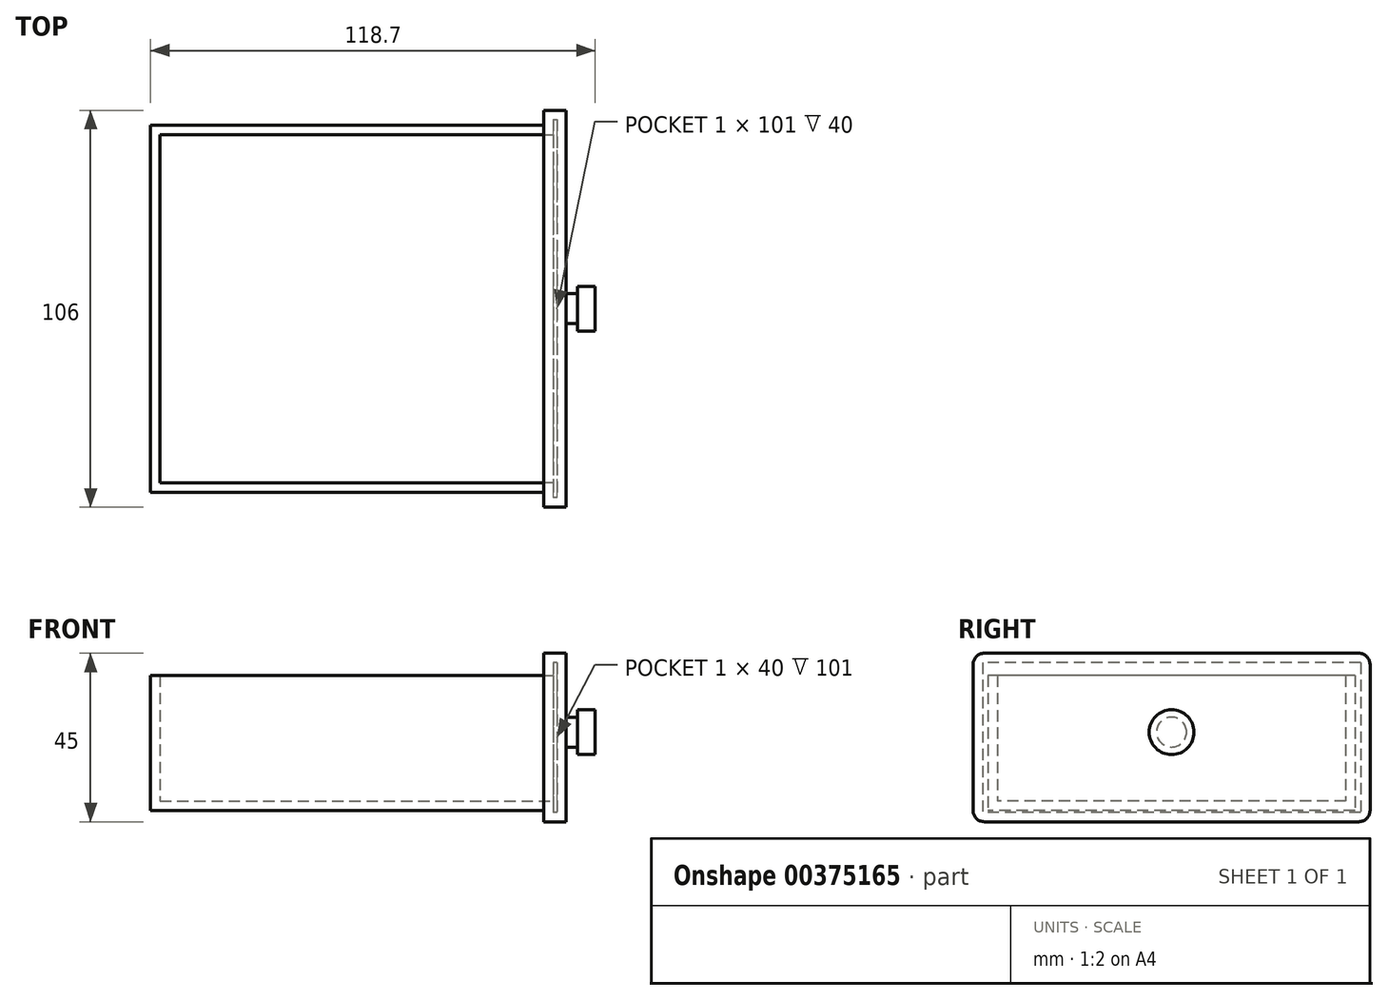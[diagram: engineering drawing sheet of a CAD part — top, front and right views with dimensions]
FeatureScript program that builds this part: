
annotation { "Feature Type Name" : "Feature", "Feature Type Description" : "" }
export const myFeature = defineFeature(function(context is Context, id is Id, definition is map)
    precondition{}
    {
        {
            var Q0;
            Q0=qCreatedBy(makeId("Top.planeOp"),FACE);
            var sketch = newSketch(context, id + "F0", { "sketchPlane" : qUnion([Q0])});
            skLineSegment(sketch, "E0", {"start": v(0, 49) * mm, "end": v(0, -49) * mm});
            skLineSegment(sketch, "E1", {"start": v(0, 49) * mm, "end": v(105, 49) * mm});
            skLineSegment(sketch, "E2", {"start": v(105, 49) * mm, "end": v(105, -49) * mm});
            skLineSegment(sketch, "E3", {"start": v(105, -49) * mm, "end": v(0, -49) * mm});
            skLineSegment(sketch, "E4", {"start": v(105, 53) * mm, "end": v(105, -53) * mm});
            skLineSegment(sketch, "E5", {"start": v(105, 53) * mm, "end": v(111, 53) * mm});
            skLineSegment(sketch, "E6", {"start": v(111, 53) * mm, "end": v(111, -53) * mm});
            skLineSegment(sketch, "E7", {"start": v(111, -53) * mm, "end": v(105, -53) * mm});
            skSolve(sketch);
        }
        {
            var Q0;
            Q0=makeQuery(id+"F0.imprint","IMPRINT",FACE,{"disambiguationData":[TD([[makeQuery(id+"F0.imprint","IMPRINT",EDGE,{"derivedFrom":sQuery(id+"F0.wireOp",EDGE,"E0")}),1.0]])]});
            extrude(context, id + "F1", {"entities" : qUnion([Q0]), "depth" : 36 * mm});
        }
        {
            var Q0;
            {var subQ0=sQuery(id+"F0.wireOp",EDGE,"E5");Q0=makeQuery(id+"F0.imprint","IMPRINT",FACE,{"disambiguationData":[TD([[makeQuery(id+"F0.imprint","IMPRINT",EDGE,{"derivedFrom":subQ0}),-1.0]])]});}
            extrude(context, id + "F2", {"entities" : qUnion([Q0]), "operationType" : NewBodyOperationType.ADD, "depth" : 42 * mm});
        }
        {
            var Q0;
            {var subQ0=sQuery(id+"F0.wireOp",EDGE,"E5");Q0=makeQuery(id+"F0.imprint","IMPRINT",FACE,{"disambiguationData":[TD([[makeQuery(id+"F0.imprint","IMPRINT",EDGE,{"derivedFrom":subQ0}),-1.0]])]});}
            extrude(context, id + "F3", {"entities" : qUnion([Q0]), "operationType" : NewBodyOperationType.ADD, "oppositeDirection" : true, "depth" : 3 * mm});
        }
        {
            var Q0;
            Q0=makeQuery(id+"F1.opExtrude","CAP_FACE",FACE,{"disambiguationData":[OSD([sQuery(id+"F0.wireOp",EDGE,"E0"),sQuery(id+"F0.wireOp",EDGE,"E1"),sQuery(id+"F0.wireOp",EDGE,"E3"),sQuery(id+"F0.wireOp",EDGE,"E4")])],"isStart":false});
            shell(context, id + "F4", {"entities" : qUnion([Q0]), "thickness" : 2.5 * mm});
        }
        {
            var Q0;
            Q0=makeQuery(id+"F2.opExtrude","CAP_EDGE",EDGE,{"disambiguationData":[OSD([sQuery(id+"F0.wireOp",EDGE,"E7")])],"isStart":false});
            var Q1;
            Q1=makeQuery(id+"F2.opExtrude","CAP_EDGE",EDGE,{"disambiguationData":[OSD([sQuery(id+"F0.wireOp",EDGE,"E5")])],"isStart":false});
            var Q2;
            Q2=makeQuery(id+"F3.opExtrude","CAP_EDGE",EDGE,{"disambiguationData":[OSD([sQuery(id+"F0.wireOp",EDGE,"E5")])],"isStart":false});
            var Q3;
            Q3=makeQuery(id+"F3.opExtrude","CAP_EDGE",EDGE,{"disambiguationData":[OSD([sQuery(id+"F0.wireOp",EDGE,"E7")])],"isStart":false});
            fillet(context, id + "F5", {"entities" : qUnion([Q0, Q1, Q2, Q3]), "radius" : 3 * mm, "tangentPropagation" : true, "allowEdgeOverflow" : false});
        }
        {
            var Q0;
            {var subQ0=sQuery(id+"F0.wireOp",EDGE,"E6");Q0=makeQuery(id+"F3.boolean.opBoolean","MERGE",FACE,{"derivedFrom":[makeQuery(id+"F2.opExtrude","SWEPT_FACE",FACE,{"disambiguationData":[OSD([subQ0])]}),makeQuery(id+"F3.opExtrude","SWEPT_FACE",FACE,{"disambiguationData":[OSD([subQ0])]})]});}
            var sketch = newSketch(context, id + "F6", { "sketchPlane" : qUnion([Q0])});
            skCircle(sketch, "E8", {"center": v(0, 20.93) * mm, "radius": 4 * mm});
            skPoint(sketch, "E8.centerSnap0", {"position": v(0, 42) * mm});
            skCircle(sketch, "E9", {"center": v(0, 20.93) * mm, "radius": 6 * mm});
            skSolve(sketch);
        }
        {
            var Q0;
            Q0=makeQuery(id+"F6.imprint","IMPRINT",FACE,{"disambiguationData":[TD([[makeQuery(id+"F6.imprint","IMPRINT",EDGE,{"derivedFrom":sQuery(id+"F6.wireOp",EDGE,"E8")}),1.0]])]});
            extrude(context, id + "F7", {"entities" : qUnion([Q0]), "operationType" : NewBodyOperationType.ADD, "depth" : 3 * mm});
        }
        {
            var Q0;
            Q0=makeQuery(id+"F7.opExtrude","CAP_FACE",FACE,{"disambiguationData":[OSD([sQuery(id+"F6.wireOp",EDGE,"E8")])],"isStart":false});
            var sketch = newSketch(context, id + "F8", { "sketchPlane" : qUnion([Q0])});
            skCircle(sketch, "E10", {"center": v(0, 20.93) * mm, "radius": 6 * mm});
            skSolve(sketch);
        }
        {
            var Q0;
            Q0 = qSketchRegion(id + "F8", true);
            extrude(context, id + "F9", {"entities" : qUnion([Q0]), "operationType" : NewBodyOperationType.ADD, "depth" : 4.7 * mm});
        }
    });
